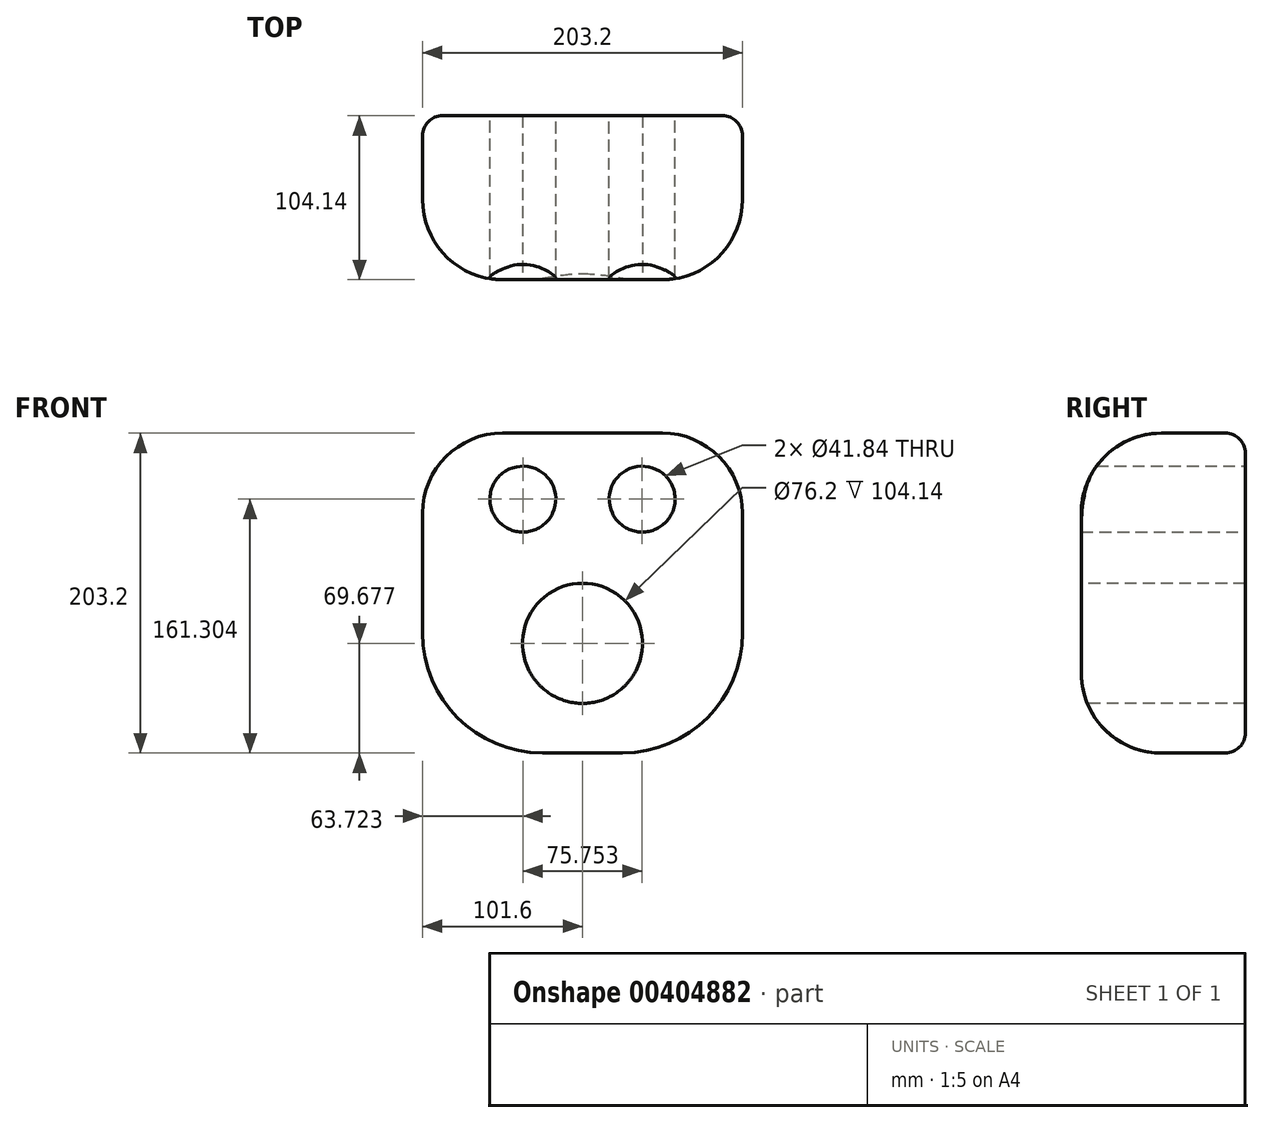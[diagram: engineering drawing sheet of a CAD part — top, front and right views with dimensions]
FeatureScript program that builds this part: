
annotation { "Feature Type Name" : "Feature", "Feature Type Description" : "" }
export const myFeature = defineFeature(function(context is Context, id is Id, definition is map)
    precondition{}
    {
        {
            var Q0;
            Q0=qCreatedBy(makeId("Front.planeOp"),FACE);
            var sketch = newSketch(context, id + "F0", { "sketchPlane" : qUnion([Q0])});
            skLineSegment(sketch, "E0.bottom", {"start": v(-50.8, 101.6) * mm, "end": v(50.8, 101.6) * mm});
            skLineSegment(sketch, "E0.top", {"start": v(-25.4, -101.6) * mm, "end": v(25.4, -101.6) * mm});
            skLineSegment(sketch, "E0.left", {"start": v(-101.6, 50.8) * mm, "end": v(-101.6, -25.4) * mm});
            skLineSegment(sketch, "E0.right", {"start": v(101.6, 50.8) * mm, "end": v(101.6, -25.4) * mm});
            skPoint(sketch, "E0.middle", {"position": v(0, 0) * mm});
            skPoint(sketch, "E1.visualSharp", {"position": v(-101.6, 101.6) * mm});
            skArc(sketch, "E1.filletArc", {"start": v(-50.8, 101.6) * mm, "mid": v(-86.72, 86.72) * mm, "end": v(-101.6, 50.8) * mm});
            skPoint(sketch, "E2.visualSharp", {"position": v(101.6, 101.6) * mm});
            skArc(sketch, "E2.filletArc", {"start": v(101.6, 50.8) * mm, "mid": v(86.72, 86.72) * mm, "end": v(50.8, 101.6) * mm});
            skPoint(sketch, "E3.visualSharp", {"position": v(-101.6, -101.6) * mm});
            skArc(sketch, "E3.filletArc", {"start": v(-101.6, -25.4) * mm, "mid": v(-79.28, -79.28) * mm, "end": v(-25.4, -101.6) * mm});
            skPoint(sketch, "E4.visualSharp", {"position": v(101.6, -101.6) * mm});
            skArc(sketch, "E4.filletArc", {"start": v(25.4, -101.6) * mm, "mid": v(79.28, -79.28) * mm, "end": v(101.6, -25.4) * mm});
            skCircle(sketch, "E5", {"center": v(-37.88, 59.7) * mm, "radius": 20.92 * mm});
            skLineSegment(sketch, "E6", {"start": v(0, 101.6) * mm, "end": v(0, -101.6) * mm});
            skCircle(sketch, "E7.MirrorC", {"center": v(37.88, 59.7) * mm, "radius": 20.92 * mm});
            skSolve(sketch);
        }
        {
            var Q0;
            Q0 = qSketchRegion(id + "F0", true);
            extrude(context, id + "F1", {"entities" : qUnion([Q0]), "depth" : 104.14 * mm});
        }
        {
            var Q0;
            Q0=makeQuery(id+"F1.opExtrude","CAP_EDGE",EDGE,{"disambiguationData":[OSD([sQuery(id+"F0.wireOp",EDGE,"E1.filletArc")])],"isStart":false});
            fillet(context, id + "F2", {"entities" : qUnion([Q0]), "radius" : 50.8 * mm, "tangentPropagation" : true, "allowEdgeOverflow" : false});
        }
        {
            var Q0;
            Q0=makeQuery(id+"F1.opExtrude","CAP_EDGE",EDGE,{"disambiguationData":[OSD([sQuery(id+"F0.wireOp",EDGE,"E1.filletArc")])],"isStart":true});
            fillet(context, id + "F3", {"entities" : qUnion([Q0]), "radius" : 12.7 * mm, "tangentPropagation" : true, "allowEdgeOverflow" : false});
        }
        {
            var Q0;
            Q0=makeQuery(id+"F1.opExtrude","CAP_FACE",FACE,{"disambiguationData":[OSD([sQuery(id+"F0.wireOp",EDGE,"E0.bottom"),sQuery(id+"F0.wireOp",EDGE,"E0.top"),sQuery(id+"F0.wireOp",EDGE,"E0.left"),sQuery(id+"F0.wireOp",EDGE,"E0.right"),sQuery(id+"F0.wireOp",EDGE,"E1.filletArc"),sQuery(id+"F0.wireOp",EDGE,"E2.filletArc"),sQuery(id+"F0.wireOp",EDGE,"E3.filletArc"),sQuery(id+"F0.wireOp",EDGE,"E4.filletArc"),sQuery(id+"F0.wireOp",EDGE,"E5"),sQuery(id+"F0.wireOp",EDGE,"E7.MirrorC")])],"isStart":false});
            var sketch = newSketch(context, id + "F4", { "sketchPlane" : qUnion([Q0])});
            skCircle(sketch, "E8", {"center": v(0, -31.92) * mm, "radius": 38.1 * mm});
            skSolve(sketch);
        }
        {
            var Q0;
            Q0 = qSketchRegion(id + "F4", true);
            extrude(context, id + "F5", {"entities" : qUnion([Q0]), "operationType" : NewBodyOperationType.REMOVE, "endBound" : BoundingType.THROUGH_ALL, "oppositeDirection" : true, "depth" : 25.4 * mm});
        }
    });
